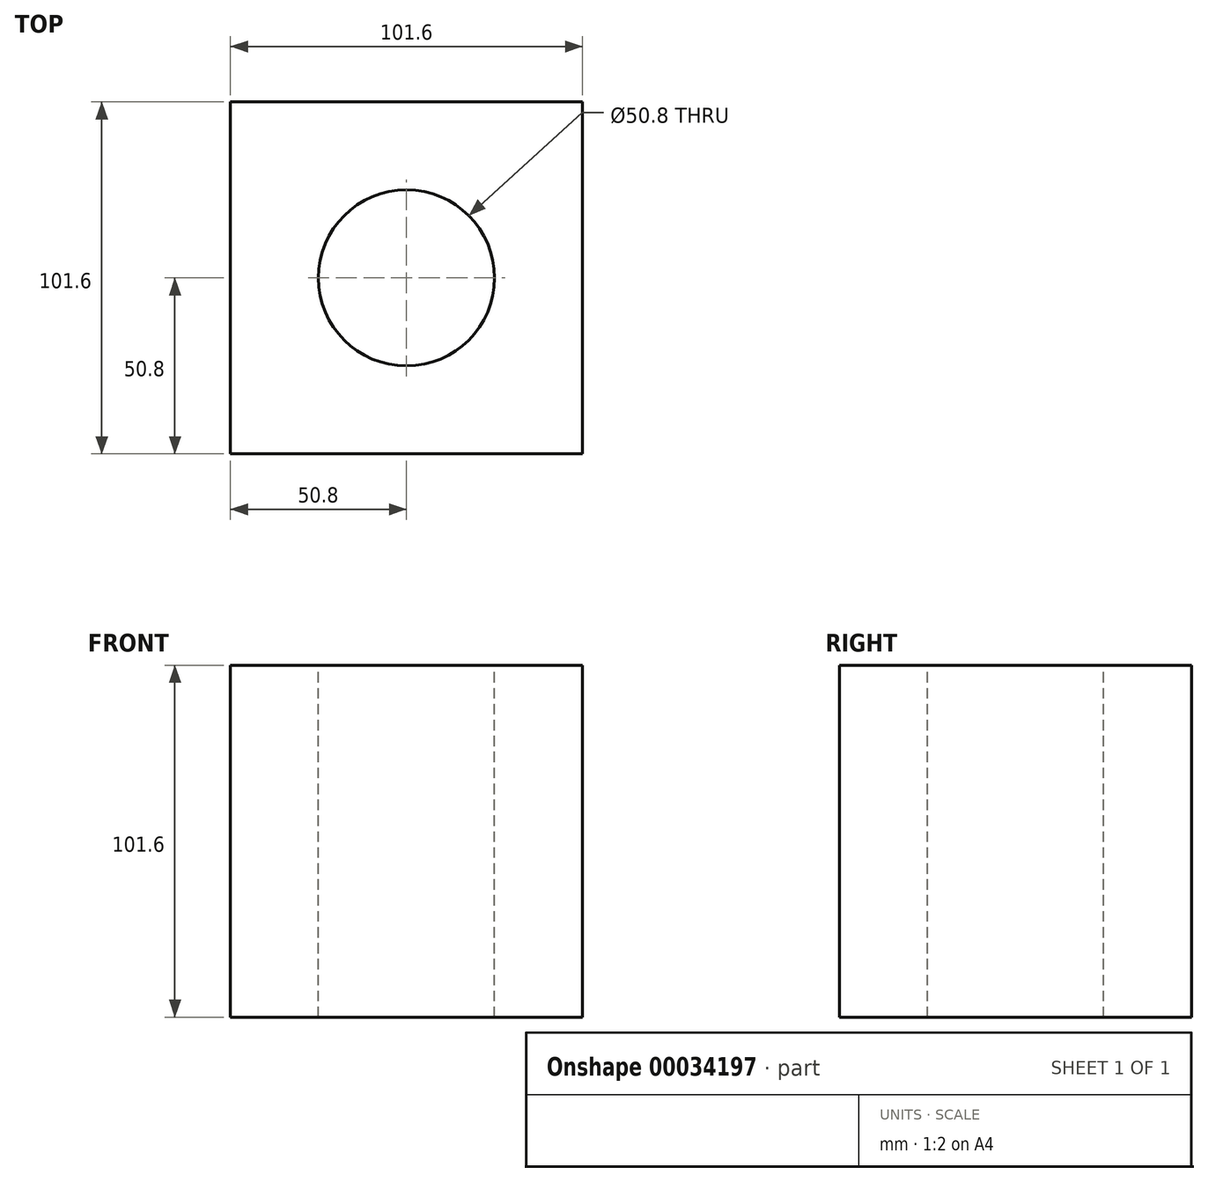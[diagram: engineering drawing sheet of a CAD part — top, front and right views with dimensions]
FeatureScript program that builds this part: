
annotation { "Feature Type Name" : "Feature", "Feature Type Description" : "" }
export const myFeature = defineFeature(function(context is Context, id is Id, definition is map)
    precondition{}
    {
        {
            var Q0;
            Q0=qCreatedBy(makeId("Front.planeOp"),FACE);
            var sketch = newSketch(context, id + "F0", { "sketchPlane" : qUnion([Q0])});
            skLineSegment(sketch, "E0.rect.bottom", {"start": v(50.8, -50.8) * mm, "end": v(-50.8, -50.8) * mm});
            skLineSegment(sketch, "E0.rect.top", {"start": v(50.8, 50.8) * mm, "end": v(-50.8, 50.8) * mm});
            skLineSegment(sketch, "E0.rect.left", {"start": v(50.8, -50.8) * mm, "end": v(50.8, 50.8) * mm});
            skLineSegment(sketch, "E0.rect.right", {"start": v(-50.8, -50.8) * mm, "end": v(-50.8, 50.8) * mm});
            skPoint(sketch, "E0.rect.middle", {"position": v(0, 0) * mm});
            skSolve(sketch);
        }
        {
            var Q0;
            Q0 = qSketchRegion(id + "F0", true);
            extrude(context, id + "F1", {"entities" : qUnion([Q0]), "endBound" : BoundingType.SYMMETRIC, "depth" : 101.6 * mm});
        }
        {
            var Q0;
            Q0=qCreatedBy(makeId("Top.planeOp"),FACE);
            var sketch = newSketch(context, id + "F2", { "sketchPlane" : qUnion([Q0])});
            skCircle(sketch, "E1", {"center": v(0, 0) * mm, "radius": 25.4 * mm});
            skSolve(sketch);
        }
        {
            var Q0;
            Q0=makeQuery(id+"F2.imprint","IMPRINT",FACE,{"disambiguationData":[TD([[makeQuery(id+"F2.imprint","IMPRINT",EDGE,{"derivedFrom":sQuery(id+"F2.wireOp",EDGE,"E1")}),1.0]])]});
            extrude(context, id + "F3", {"entities" : qUnion([Q0]), "operationType" : NewBodyOperationType.REMOVE, "endBound" : BoundingType.SYMMETRIC, "oppositeDirection" : true, "depth" : 101.6 * mm, "hasSecondDirection" : true, "secondDirectionBound" : SecondDirectionBoundingType.THROUGH_ALL, "secondDirectionOppositeDirection" : true, "secondDirectionDepth" : 25.4 * mm});
        }
    });
